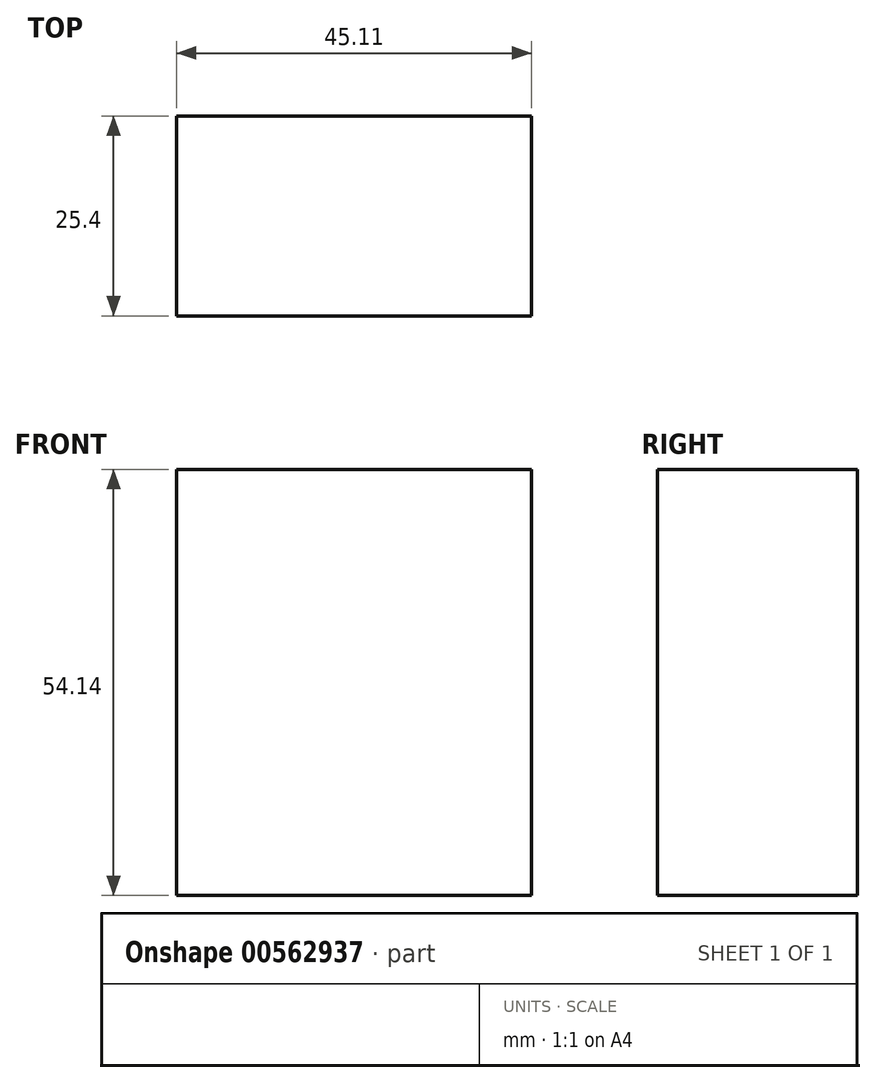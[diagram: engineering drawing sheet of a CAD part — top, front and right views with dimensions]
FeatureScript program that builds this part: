
annotation { "Feature Type Name" : "Feature", "Feature Type Description" : "" }
export const myFeature = defineFeature(function(context is Context, id is Id, definition is map)
    precondition{}
    {
        {
            var Q0;
            Q0=qCreatedBy(makeId("Front.planeOp"),FACE);
            var sketch = newSketch(context, id + "F0", { "sketchPlane" : qUnion([Q0])});
            skLineSegment(sketch, "E0.bottom", {"start": v(0, 0) * mm, "end": v(0, 0) * mm});
            skLineSegment(sketch, "E0.top", {"start": v(0, 0) * mm, "end": v(0, 0) * mm});
            skLineSegment(sketch, "E0.left", {"start": v(0, 0) * mm, "end": v(0, 0) * mm});
            skLineSegment(sketch, "E0.right", {"start": v(0, 0) * mm, "end": v(0, 0) * mm});
            skLineSegment(sketch, "E1.bottom", {"start": v(0, 0) * mm, "end": v(-45.11, 0) * mm});
            skLineSegment(sketch, "E1.top", {"start": v(0, 54.14) * mm, "end": v(-45.11, 54.14) * mm});
            skLineSegment(sketch, "E1.left", {"start": v(0, 0) * mm, "end": v(0, 54.14) * mm});
            skLineSegment(sketch, "E1.right", {"start": v(-45.11, 0) * mm, "end": v(-45.11, 54.14) * mm});
            skSolve(sketch);
        }
        {
            var Q0;
            Q0=makeQuery(id+"F0.imprint","IMPRINT",FACE,{"disambiguationData":[TD([[makeQuery(id+"F0.imprint","IMPRINT",EDGE,{"derivedFrom":sQuery(id+"F0.wireOp",EDGE,"E1.bottom")}),-1.0]])]});
            extrude(context, id + "F1", {"entities" : qUnion([Q0]), "depth" : 25.4 * mm, "offsetDistance" : 25.4 * mm});
        }
    });
